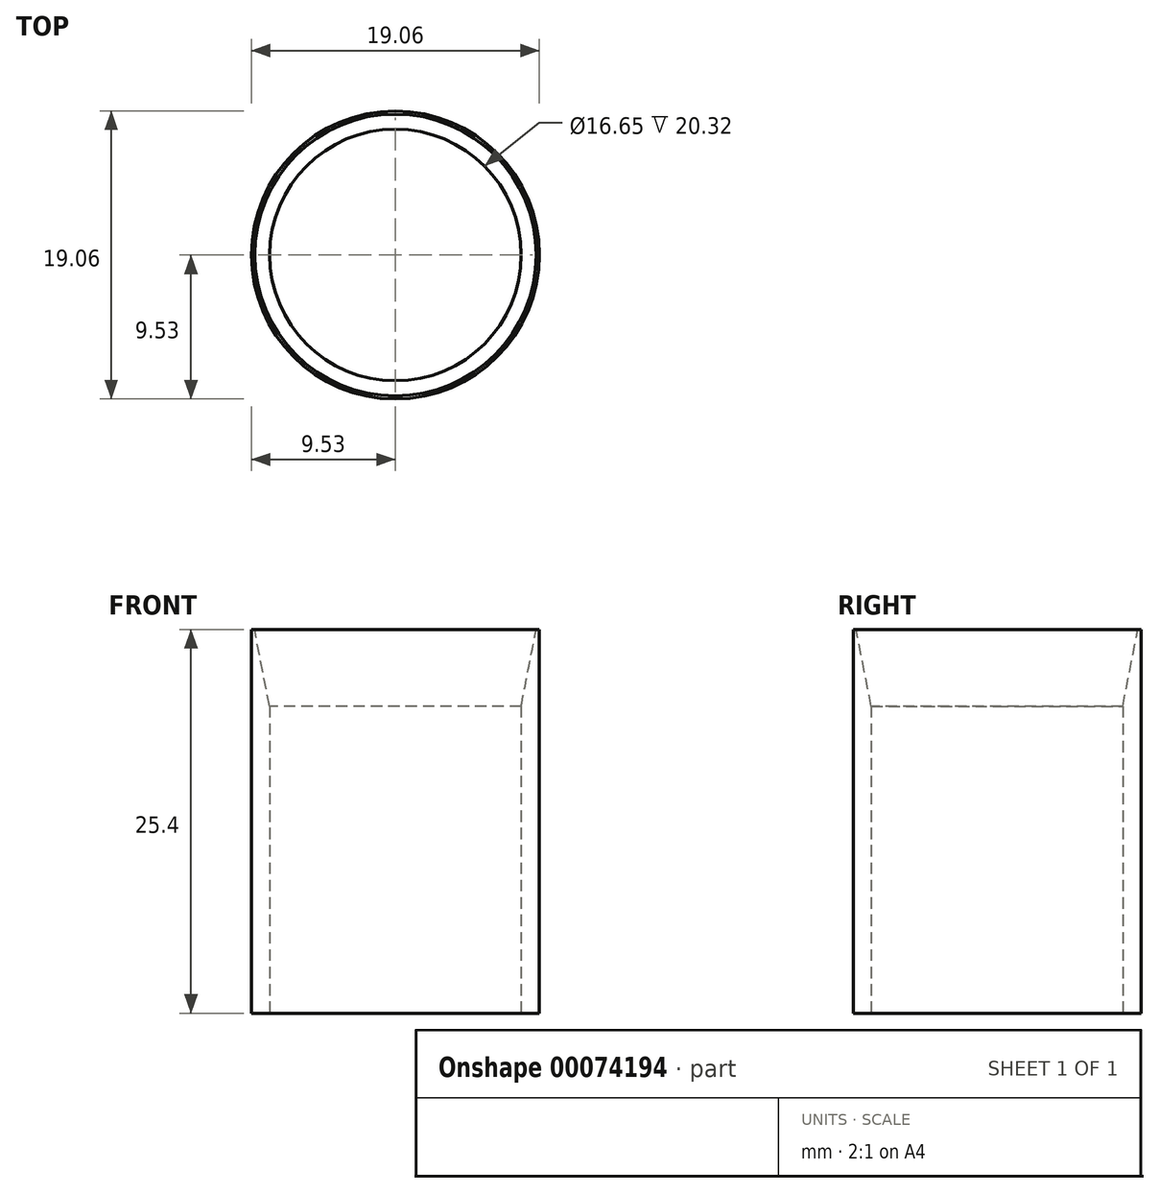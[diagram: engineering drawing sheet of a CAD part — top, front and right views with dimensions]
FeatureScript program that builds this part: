
annotation { "Feature Type Name" : "Feature", "Feature Type Description" : "" }
export const myFeature = defineFeature(function(context is Context, id is Id, definition is map)
    precondition{}
    {
        {
            var Q0;
            Q0=qCreatedBy(makeId("Top.planeOp"),FACE);
            var sketch = newSketch(context, id + "F0", { "sketchPlane" : qUnion([Q0])});
            skCircle(sketch, "E0", {"center": v(0, 0) * mm, "radius": 9.53 * mm});
            skSolve(sketch);
        }
        {
            var Q0;
            Q0=makeQuery(id+"F0.imprint","IMPRINT",FACE,{"disambiguationData":[TD([[makeQuery(id+"F0.imprint","IMPRINT",EDGE,{"derivedFrom":sQuery(id+"F0.wireOp",EDGE,"E0")}),1.0]])]});
            extrude(context, id + "F1", {"entities" : qUnion([Q0]), "depth" : 25.4 * mm});
        }
        {
            var Q0;
            Q0=makeQuery(id+"F1.opExtrude","CAP_FACE",FACE,{"disambiguationData":[OSD([sQuery(id+"F0.wireOp",EDGE,"E0")])],"isStart":false});
            var Q1;
            Q1=makeQuery(id+"F1.opExtrude","CAP_FACE",FACE,{"disambiguationData":[OSD([sQuery(id+"F0.wireOp",EDGE,"E0")])],"isStart":true});
            shell(context, id + "F2", {"entities" : qUnion([Q0, Q1]), "thickness" : 1.2 * mm});
        }
        {
            var Q0;
            {var subQ0=sQuery(id+"F0.wireOp",EDGE,"E0");Q0=makeQuery(id+"F2.opShell","OFFSET_EDGE",EDGE,{"disambiguationData":[OSD([subQ0]),TDD([makeQuery(id+"F1.opExtrude","CAP_EDGE",EDGE,{"disambiguationData":[OSD([subQ0])],"isStart":false})])]});}
            chamfer(context, id + "F3", {"entities" : qUnion([Q0]), "chamferType" : ChamferType.OFFSET_ANGLE, "width" : 5.08 * mm, "oppositeDirection" : false, "angle" : 11.1 * degree, "tangentPropagation" : true});
        }
    });
